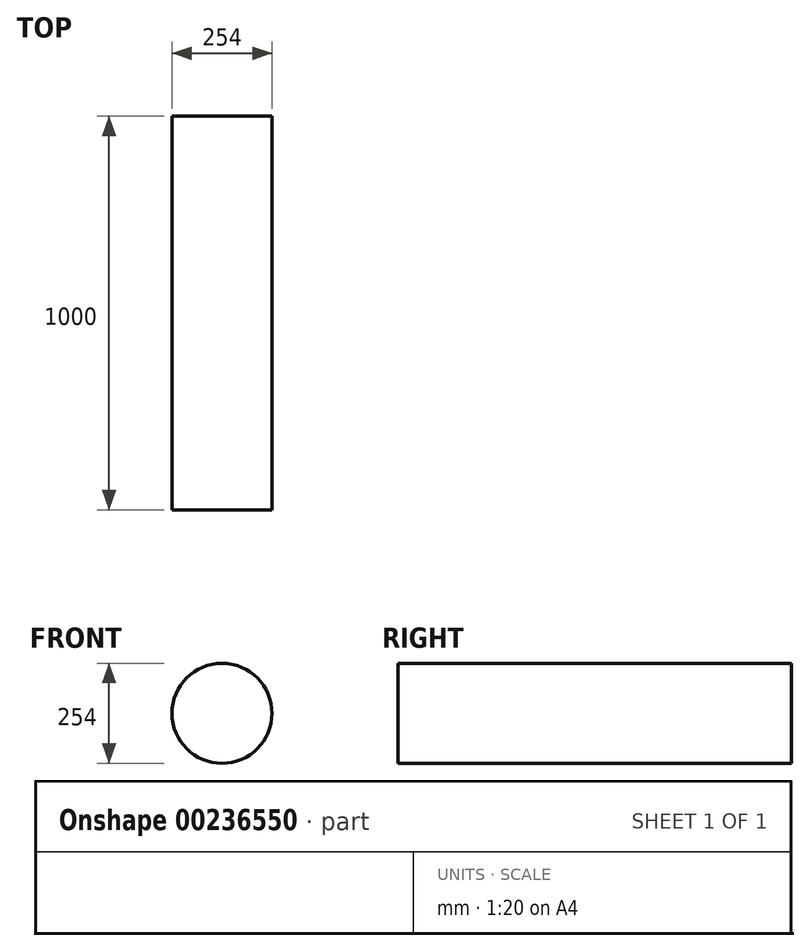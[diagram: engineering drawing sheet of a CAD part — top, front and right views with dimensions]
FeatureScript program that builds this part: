
annotation { "Feature Type Name" : "Feature", "Feature Type Description" : "" }
export const myFeature = defineFeature(function(context is Context, id is Id, definition is map)
    precondition{}
    {
        {
            var Q0;
            Q0=qCreatedBy(makeId("Front.planeOp"),FACE);
            var sketch = newSketch(context, id + "F0", { "sketchPlane" : qUnion([Q0])});
            skCircle(sketch, "E0", {"center": v(0, 0) * mm, "radius": 127 * mm});
            skSolve(sketch);
        }
        {
            var Q0;
            Q0=makeQuery(id+"F0.imprint","IMPRINT",FACE,{"disambiguationData":[TD([[makeQuery(id+"F0.imprint","IMPRINT",EDGE,{"derivedFrom":sQuery(id+"F0.wireOp",EDGE,"E0")}),1.0]])]});
            extrude(context, id + "F1", {"entities" : qUnion([Q0]), "depth" : 1000 * mm});
        }
    });
